# Revit family: Enna Wall LED
name_source: partatom
category: Lighting Fixtures
revit_build: Autodesk Revit 2017 (Build: 20160225_1515(x64)
units: mm (PartAtom-declared; Revit-internal decimal feet)

## family parameters
Always vertical = Yes
Cut with Voids When Loaded = No
Host = Wall
Light Source = Yes
OmniClass Number = 23.80.70.00
OmniClass Title = Lighting
Part Type = Normal
Room Calculation Point = No
Round Connector Dimension = Use Diameter
Shared = No

## types (2) — shared parameters
Color Filter = 16777215
Dimming Lamp Color Temperature Shift = <None>
Driver Required = No
Emit from Line Length = 610 mm
Light Source Symbol Size = 610 mm
Main Material = Metal - Steel
Manufacturer = Astro Lighting Ltd
Product Code = 1234
Product SKU = 1234001
URL = www.astrolighting.com
zero-valued in all types: Electrical Class

## per-type parameters (varying)
| type | ADA compliant | Location rating | Product Location |
| CE |  |  |  |
| ETL | NO | DAMP | Bathroom |

## geometry (parser evidence)
native form markers: Sweep x3
no freeform markers — native parametric forms only
